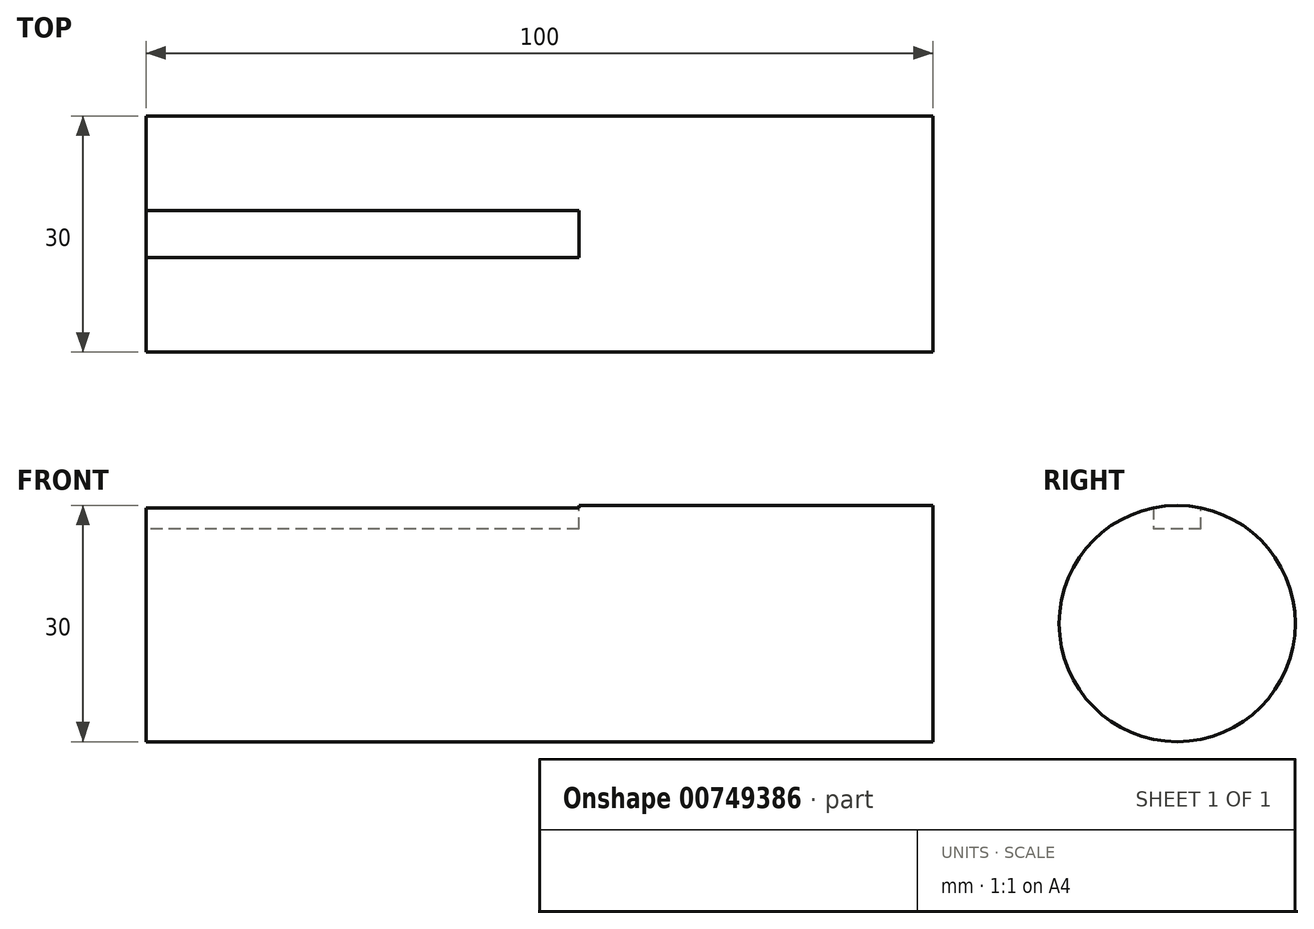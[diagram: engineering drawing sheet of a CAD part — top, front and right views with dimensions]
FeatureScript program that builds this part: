
annotation { "Feature Type Name" : "Feature", "Feature Type Description" : "" }
export const myFeature = defineFeature(function(context is Context, id is Id, definition is map)
    precondition{}
    {
        {
            var Q0;
            Q0=qCreatedBy(makeId("Front.planeOp"),FACE);
            var sketch = newSketch(context, id + "F0", { "sketchPlane" : qUnion([Q0])});
            skLineSegment(sketch, "E0", {"start": v(-50, 0) * mm, "end": v(-50, 15) * mm});
            skLineSegment(sketch, "E1", {"start": v(-50, 15) * mm, "end": v(50, 15) * mm});
            skLineSegment(sketch, "E2", {"start": v(50, 15) * mm, "end": v(50, 0) * mm});
            skLineSegment(sketch, "E3", {"start": v(-50, 0) * mm, "end": v(50, 0) * mm});
            skSolve(sketch);
        }
        {
            var Q0;
            Q0=makeQuery(id+"F0.imprint","IMPRINT",FACE,{"disambiguationData":[TD([[makeQuery(id+"F0.imprint","IMPRINT",EDGE,{"derivedFrom":sQuery(id+"F0.wireOp",EDGE,"E0")}),-1.0]])]});
            var Q1;
            Q1=sQuery(id+"F0.wireOp",EDGE,"E3");
            revolve(context, id + "F1", {"surfaceOperationType" : NewSurfaceOperationType.NEW, "entities" : qUnion([Q0]), "axis" : qUnion([Q1]), "revolveType" : RevolveType.FULL});
        }
        {
            var Q0;
            Q0=makeQuery(id+"F1.opRevolve","SWEPT_FACE",FACE,{"disambiguationData":[OSD([sQuery(id+"F0.wireOp",EDGE,"E0")])]});
            var sketch = newSketch(context, id + "F2", { "sketchPlane" : qUnion([Q0])});
            skArc(sketch, "E4", {"start": v(3, 14.7) * mm, "mid": v(0, 15) * mm, "end": v(-3, 14.7) * mm});
            skLineSegment(sketch, "E5", {"start": v(-3, 12) * mm, "end": v(-3, 14.7) * mm});
            skLineSegment(sketch, "E6", {"start": v(3, 14.7) * mm, "end": v(3, 12) * mm});
            skLineSegment(sketch, "E7", {"start": v(-3, 12) * mm, "end": v(3, 12) * mm});
            skSolve(sketch);
        }
        {
            var Q0;
            Q0=makeQuery(id+"F2.imprint","IMPRINT",FACE,{"disambiguationData":[TD([[makeQuery(id+"F2.imprint","IMPRINT",EDGE,{"derivedFrom":sQuery(id+"F2.wireOp",EDGE,"E4")}),1.0]])]});
            extrude(context, id + "F3", {"entities" : qUnion([Q0]), "operationType" : NewBodyOperationType.REMOVE, "oppositeDirection" : true, "depth" : 55 * mm, "offsetDistance" : 25 * mm});
        }
    });
